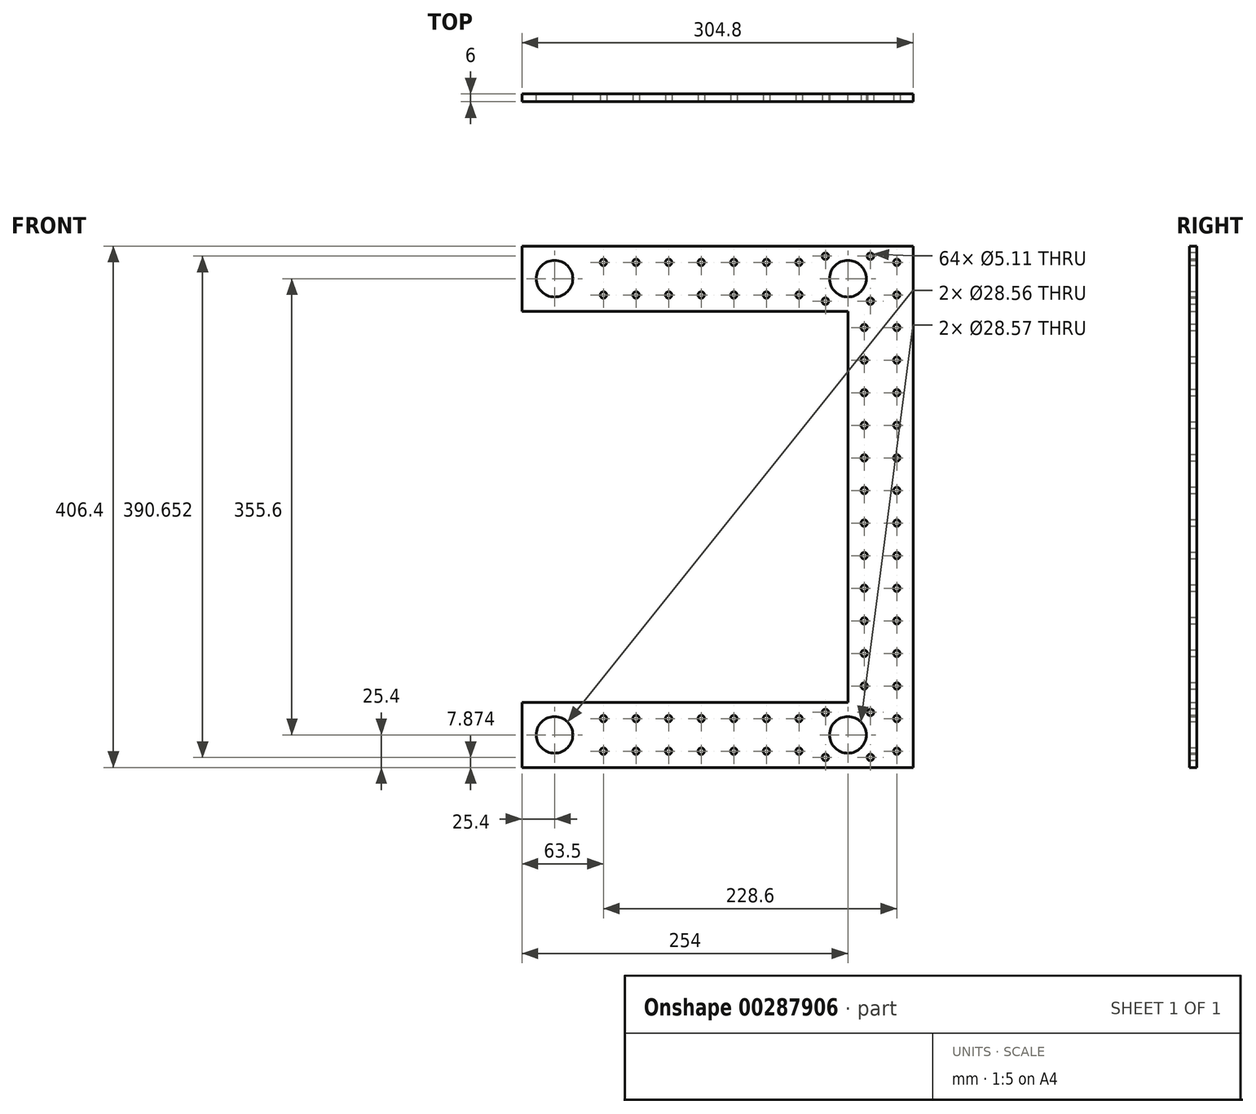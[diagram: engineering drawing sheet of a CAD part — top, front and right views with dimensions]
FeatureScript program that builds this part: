
annotation { "Feature Type Name" : "Feature", "Feature Type Description" : "" }
export const myFeature = defineFeature(function(context is Context, id is Id, definition is map)
    precondition{}
    {
        {
            var Q0;
            Q0=qCreatedBy(makeId("Front.planeOp"),FACE);
            var sketch = newSketch(context, id + "F0", { "sketchPlane" : qUnion([Q0])});
            skCircle(sketch, "E0", {"center": v(0, 0) * mm, "radius": 152.4 * mm, "construction": true});
            skLineSegment(sketch, "E1", {"start": v(0, 0) * mm, "end": v(177.8, 0) * mm, "construction": true});
            skLineSegment(sketch, "E2.bottom", {"start": v(203.2, 152.4) * mm, "end": v(152.4, 152.4) * mm, "construction": true});
            skLineSegment(sketch, "E2.top", {"start": v(203.2, -152.4) * mm, "end": v(152.4, -152.4) * mm, "construction": true});
            skLineSegment(sketch, "E2.left", {"start": v(203.2, 152.4) * mm, "end": v(203.2, -152.4) * mm});
            skLineSegment(sketch, "E2.right", {"start": v(152.4, 152.4) * mm, "end": v(152.4, -152.4) * mm});
            skPoint(sketch, "E2.middle", {"position": v(177.8, 0) * mm});
            skLineSegment(sketch, "E3", {"start": v(203.2, -152.4) * mm, "end": v(203.2, -203.2) * mm});
            skLineSegment(sketch, "E4", {"start": v(203.2, -203.2) * mm, "end": v(-101.6, -203.2) * mm});
            skLineSegment(sketch, "E5", {"start": v(-101.6, -203.2) * mm, "end": v(-101.6, -152.4) * mm});
            skLineSegment(sketch, "E6", {"start": v(-101.6, -152.4) * mm, "end": v(152.4, -152.4) * mm});
            skCircle(sketch, "E7", {"center": v(-76.2, -177.8) * mm, "radius": 14.28 * mm});
            skCircle(sketch, "E8", {"center": v(-76.2, -177.8) * mm, "radius": 38.1 * mm, "construction": true});
            skLineSegment(sketch, "E9.MirrorCS", {"start": v(-101.6, 152.4) * mm, "end": v(152.4, 152.4) * mm});
            skLineSegment(sketch, "E10.MirrorCS", {"start": v(203.2, 203.2) * mm, "end": v(-101.6, 203.2) * mm});
            skLineSegment(sketch, "E11.MirrorCS", {"start": v(203.2, 152.4) * mm, "end": v(203.2, 203.2) * mm});
            skCircle(sketch, "E12.MirrorC", {"center": v(-76.2, 177.8) * mm, "radius": 14.28 * mm});
            skCircle(sketch, "E13.MirrorC", {"center": v(-76.2, 177.8) * mm, "radius": 38.1 * mm, "construction": true});
            skLineSegment(sketch, "E14.MirrorCS", {"start": v(-101.6, 203.2) * mm, "end": v(-101.6, 152.4) * mm});
            skSolve(sketch);
        }
        {
            var Q0;
            Q0 = qSketchRegion(id + "F0", true);
            extrude(context, id + "F1", {"entities" : qUnion([Q0]), "depth" : 6 * mm});
        }
        {
            var Q0;
            Q0=makeQuery(id+"F1.opExtrude","CAP_FACE",FACE,{"disambiguationData":[OSD([sQuery(id+"F0.wireOp",EDGE,"E2.left"),sQuery(id+"F0.wireOp",EDGE,"E2.right"),sQuery(id+"F0.wireOp",EDGE,"E3"),sQuery(id+"F0.wireOp",EDGE,"E4"),sQuery(id+"F0.wireOp",EDGE,"E5"),sQuery(id+"F0.wireOp",EDGE,"E6"),sQuery(id+"F0.wireOp",EDGE,"E7"),sQuery(id+"F0.wireOp",EDGE,"E9.MirrorCS"),sQuery(id+"F0.wireOp",EDGE,"E10.MirrorCS"),sQuery(id+"F0.wireOp",EDGE,"E11.MirrorCS"),sQuery(id+"F0.wireOp",EDGE,"E12.MirrorC"),sQuery(id+"F0.wireOp",EDGE,"E14.MirrorCS")])],"isStart":false});
            var sketch = newSketch(context, id + "F2", { "sketchPlane" : qUnion([Q0])});
            skLineSegment(sketch, "E15", {"start": v(0, 0) * mm, "end": v(152.4, 0) * mm, "construction": true});
            skLineSegment(sketch, "E16", {"start": v(152.4, 152.4) * mm, "end": v(152.4, 203.2) * mm, "construction": true});
            skCircle(sketch, "E17", {"center": v(152.4, 177.8) * mm, "radius": 14.29 * mm});
            skLineSegment(sketch, "E18.bottom", {"start": v(169.93, 160.27) * mm, "end": v(134.87, 160.27) * mm, "construction": true});
            skLineSegment(sketch, "E18.top", {"start": v(169.93, 195.33) * mm, "end": v(134.87, 195.33) * mm, "construction": true});
            skLineSegment(sketch, "E18.left", {"start": v(169.93, 160.27) * mm, "end": v(169.93, 195.33) * mm, "construction": true});
            skLineSegment(sketch, "E18.right", {"start": v(134.87, 160.27) * mm, "end": v(134.87, 195.33) * mm, "construction": true});
            skCircle(sketch, "E19", {"center": v(169.93, 195.33) * mm, "radius": 2.55 * mm});
            skCircle(sketch, "E20", {"center": v(169.93, 160.27) * mm, "radius": 2.55 * mm});
            skCircle(sketch, "E21", {"center": v(134.87, 160.27) * mm, "radius": 2.55 * mm});
            skCircle(sketch, "E22", {"center": v(134.87, 195.33) * mm, "radius": 2.55 * mm});
            skCircle(sketch, "E23.MirrorC", {"center": v(134.87, -195.33) * mm, "radius": 2.55 * mm});
            skCircle(sketch, "E24.MirrorC", {"center": v(134.87, -160.27) * mm, "radius": 2.55 * mm});
            skLineSegment(sketch, "E25.MirrorCS", {"start": v(169.93, -195.33) * mm, "end": v(134.87, -195.33) * mm, "construction": true});
            skLineSegment(sketch, "E26.MirrorCS", {"start": v(169.93, -160.27) * mm, "end": v(134.87, -160.27) * mm, "construction": true});
            skCircle(sketch, "E27.MirrorC", {"center": v(169.93, -160.27) * mm, "radius": 2.55 * mm});
            skCircle(sketch, "E28.MirrorC", {"center": v(152.4, -177.8) * mm, "radius": 14.29 * mm});
            skLineSegment(sketch, "E29.MirrorCS", {"start": v(134.87, -160.27) * mm, "end": v(134.87, -195.33) * mm, "construction": true});
            skCircle(sketch, "E30.MirrorC", {"center": v(169.93, -195.33) * mm, "radius": 2.55 * mm});
            skLineSegment(sketch, "E31.MirrorCS", {"start": v(152.4, -152.4) * mm, "end": v(152.4, -203.2) * mm, "construction": true});
            skLineSegment(sketch, "E32.MirrorCS", {"start": v(169.93, -160.27) * mm, "end": v(169.93, -195.33) * mm, "construction": true});
            skSolve(sketch);
        }
        {
            var Q0;
            Q0 = qSketchRegion(id + "F2", true);
            extrude(context, id + "F3", {"entities" : qUnion([Q0]), "operationType" : NewBodyOperationType.REMOVE, "oppositeDirection" : true, "depth" : 25.4 * mm});
        }
        {
            var Q0;
            Q0=makeQuery(id+"F1.opExtrude","CAP_FACE",FACE,{"disambiguationData":[OSD([sQuery(id+"F0.wireOp",EDGE,"E2.left"),sQuery(id+"F0.wireOp",EDGE,"E2.right"),sQuery(id+"F0.wireOp",EDGE,"E3"),sQuery(id+"F0.wireOp",EDGE,"E4"),sQuery(id+"F0.wireOp",EDGE,"E5"),sQuery(id+"F0.wireOp",EDGE,"E6"),sQuery(id+"F0.wireOp",EDGE,"E7"),sQuery(id+"F0.wireOp",EDGE,"E9.MirrorCS"),sQuery(id+"F0.wireOp",EDGE,"E10.MirrorCS"),sQuery(id+"F0.wireOp",EDGE,"E11.MirrorCS"),sQuery(id+"F0.wireOp",EDGE,"E12.MirrorC"),sQuery(id+"F0.wireOp",EDGE,"E14.MirrorCS")])],"isStart":false});
            var sketch = newSketch(context, id + "F4", { "sketchPlane" : qUnion([Q0])});
            skCircle(sketch, "E33", {"center": v(-88.9, 190.5) * mm, "radius": 2.55 * mm, "construction": true});
            skCircle(sketch, "E34.0.1.0", {"center": v(-88.9, 165.1) * mm, "radius": 2.55 * mm, "construction": true});
            skCircle(sketch, "E34.1.0.0", {"center": v(-63.5, 190.5) * mm, "radius": 2.55 * mm, "construction": true});
            skCircle(sketch, "E34.1.1.0", {"center": v(-63.5, 165.1) * mm, "radius": 2.55 * mm, "construction": true});
            skCircle(sketch, "E34.2.0.0", {"center": v(-38.1, 190.5) * mm, "radius": 2.55 * mm});
            skCircle(sketch, "E34.2.1.0", {"center": v(-38.1, 165.1) * mm, "radius": 2.55 * mm});
            skCircle(sketch, "E34.3.0.0", {"center": v(-12.7, 190.5) * mm, "radius": 2.55 * mm});
            skCircle(sketch, "E34.3.1.0", {"center": v(-12.7, 165.1) * mm, "radius": 2.55 * mm});
            skCircle(sketch, "E34.4.0.0", {"center": v(12.7, 190.5) * mm, "radius": 2.55 * mm});
            skCircle(sketch, "E34.4.1.0", {"center": v(12.7, 165.1) * mm, "radius": 2.55 * mm});
            skCircle(sketch, "E34.5.0.0", {"center": v(38.1, 190.5) * mm, "radius": 2.55 * mm});
            skCircle(sketch, "E34.5.1.0", {"center": v(38.1, 165.1) * mm, "radius": 2.55 * mm});
            skCircle(sketch, "E34.6.0.0", {"center": v(63.5, 190.5) * mm, "radius": 2.55 * mm});
            skCircle(sketch, "E34.6.1.0", {"center": v(63.5, 165.1) * mm, "radius": 2.55 * mm});
            skCircle(sketch, "E34.7.0.0", {"center": v(88.9, 190.5) * mm, "radius": 2.55 * mm});
            skCircle(sketch, "E34.7.1.0", {"center": v(88.9, 165.1) * mm, "radius": 2.55 * mm});
            skCircle(sketch, "E34.8.0.0", {"center": v(114.3, 190.5) * mm, "radius": 2.55 * mm});
            skCircle(sketch, "E34.8.1.0", {"center": v(114.3, 165.1) * mm, "radius": 2.55 * mm});
            skCircle(sketch, "E34.9.0.0", {"center": v(139.7, 190.5) * mm, "radius": 2.55 * mm, "construction": true});
            skCircle(sketch, "E34.9.1.0", {"center": v(139.7, 165.1) * mm, "radius": 2.55 * mm, "construction": true});
            skCircle(sketch, "E34.10.0.0", {"center": v(165.1, 190.5) * mm, "radius": 2.55 * mm, "construction": true});
            skCircle(sketch, "E34.10.1.0", {"center": v(165.1, 165.1) * mm, "radius": 2.55 * mm, "construction": true});
            skCircle(sketch, "E34.11.0.0", {"center": v(190.5, 190.5) * mm, "radius": 2.55 * mm});
            skCircle(sketch, "E34.11.1.0", {"center": v(190.5, 165.1) * mm, "radius": 2.55 * mm});
            skLineSegment(sketch, "E34.direction1", {"start": v(-88.9, 190.5) * mm, "end": v(-63.5, 190.5) * mm, "construction": true});
            skLineSegment(sketch, "E34.direction2", {"start": v(-88.9, 190.5) * mm, "end": v(-88.9, 165.1) * mm, "construction": true});
            skLineSegment(sketch, "E35", {"start": v(0, 0) * mm, "end": v(152.4, 0) * mm, "construction": true});
            skCircle(sketch, "E36.MirrorC", {"center": v(165.1, -165.1) * mm, "radius": 2.55 * mm, "construction": true});
            skCircle(sketch, "E37.MirrorC", {"center": v(-88.9, -190.5) * mm, "radius": 2.55 * mm, "construction": true});
            skCircle(sketch, "E38.MirrorC", {"center": v(88.9, -190.5) * mm, "radius": 2.55 * mm});
            skCircle(sketch, "E39.MirrorC", {"center": v(-38.1, -190.5) * mm, "radius": 2.55 * mm});
            skCircle(sketch, "E40.MirrorC", {"center": v(139.7, -190.5) * mm, "radius": 2.55 * mm, "construction": true});
            skLineSegment(sketch, "E41.MirrorCS", {"start": v(-88.9, -190.5) * mm, "end": v(-63.5, -190.5) * mm, "construction": true});
            skCircle(sketch, "E42.MirrorC", {"center": v(38.1, -190.5) * mm, "radius": 2.55 * mm});
            skCircle(sketch, "E43.MirrorC", {"center": v(-88.9, -165.1) * mm, "radius": 2.55 * mm, "construction": true});
            skCircle(sketch, "E44.MirrorC", {"center": v(88.9, -165.1) * mm, "radius": 2.55 * mm});
            skCircle(sketch, "E45.MirrorC", {"center": v(-12.7, -165.1) * mm, "radius": 2.55 * mm});
            skCircle(sketch, "E46.MirrorC", {"center": v(-38.1, -165.1) * mm, "radius": 2.55 * mm});
            skCircle(sketch, "E47.MirrorC", {"center": v(165.1, -190.5) * mm, "radius": 2.55 * mm, "construction": true});
            skCircle(sketch, "E48.MirrorC", {"center": v(38.1, -165.1) * mm, "radius": 2.55 * mm});
            skCircle(sketch, "E49.MirrorC", {"center": v(-63.5, -190.5) * mm, "radius": 2.55 * mm, "construction": true});
            skCircle(sketch, "E50.MirrorC", {"center": v(114.3, -165.1) * mm, "radius": 2.55 * mm});
            skCircle(sketch, "E51.MirrorC", {"center": v(190.5, -190.5) * mm, "radius": 2.55 * mm});
            skCircle(sketch, "E52.MirrorC", {"center": v(190.5, -165.1) * mm, "radius": 2.55 * mm});
            skCircle(sketch, "E53.MirrorC", {"center": v(12.7, -190.5) * mm, "radius": 2.55 * mm});
            skCircle(sketch, "E54.MirrorC", {"center": v(-12.7, -190.5) * mm, "radius": 2.55 * mm});
            skCircle(sketch, "E55.MirrorC", {"center": v(63.5, -165.1) * mm, "radius": 2.55 * mm});
            skCircle(sketch, "E56.MirrorC", {"center": v(139.7, -165.1) * mm, "radius": 2.55 * mm, "construction": true});
            skCircle(sketch, "E57.MirrorC", {"center": v(63.5, -190.5) * mm, "radius": 2.55 * mm});
            skLineSegment(sketch, "E58.MirrorCS", {"start": v(-88.9, -190.5) * mm, "end": v(-88.9, -165.1) * mm, "construction": true});
            skCircle(sketch, "E59.MirrorC", {"center": v(-63.5, -165.1) * mm, "radius": 2.55 * mm, "construction": true});
            skCircle(sketch, "E60.MirrorC", {"center": v(12.7, -165.1) * mm, "radius": 2.55 * mm});
            skCircle(sketch, "E61.MirrorC", {"center": v(114.3, -190.5) * mm, "radius": 2.55 * mm});
            skCircle(sketch, "E62.0.1.0", {"center": v(190.5, 139.7) * mm, "radius": 2.55 * mm});
            skCircle(sketch, "E62.0.2.0", {"center": v(190.5, 114.3) * mm, "radius": 2.55 * mm});
            skCircle(sketch, "E62.0.3.0", {"center": v(190.5, 88.9) * mm, "radius": 2.55 * mm});
            skCircle(sketch, "E62.0.4.0", {"center": v(190.5, 63.5) * mm, "radius": 2.55 * mm});
            skCircle(sketch, "E62.0.5.0", {"center": v(190.5, 38.1) * mm, "radius": 2.55 * mm});
            skCircle(sketch, "E62.0.6.0", {"center": v(190.5, 12.7) * mm, "radius": 2.55 * mm});
            skCircle(sketch, "E62.0.7.0", {"center": v(190.5, -12.7) * mm, "radius": 2.55 * mm});
            skCircle(sketch, "E62.0.8.0", {"center": v(190.5, -38.1) * mm, "radius": 2.55 * mm});
            skCircle(sketch, "E62.0.9.0", {"center": v(190.5, -63.5) * mm, "radius": 2.55 * mm});
            skCircle(sketch, "E62.0.10.0", {"center": v(190.5, -88.9) * mm, "radius": 2.55 * mm});
            skCircle(sketch, "E62.0.11.0", {"center": v(190.5, -114.3) * mm, "radius": 2.55 * mm});
            skCircle(sketch, "E62.0.12.0", {"center": v(190.5, -139.7) * mm, "radius": 2.55 * mm});
            skCircle(sketch, "E62.1.0.0", {"center": v(165.1, 165.1) * mm, "radius": 2.55 * mm});
            skCircle(sketch, "E62.1.1.0", {"center": v(165.1, 139.7) * mm, "radius": 2.55 * mm});
            skCircle(sketch, "E62.1.2.0", {"center": v(165.1, 114.3) * mm, "radius": 2.55 * mm});
            skCircle(sketch, "E62.1.3.0", {"center": v(165.1, 88.9) * mm, "radius": 2.55 * mm});
            skCircle(sketch, "E62.1.4.0", {"center": v(165.1, 63.5) * mm, "radius": 2.55 * mm});
            skCircle(sketch, "E62.1.5.0", {"center": v(165.1, 38.1) * mm, "radius": 2.55 * mm});
            skCircle(sketch, "E62.1.6.0", {"center": v(165.1, 12.7) * mm, "radius": 2.55 * mm});
            skCircle(sketch, "E62.1.7.0", {"center": v(165.1, -12.7) * mm, "radius": 2.55 * mm});
            skCircle(sketch, "E62.1.8.0", {"center": v(165.1, -38.1) * mm, "radius": 2.55 * mm});
            skCircle(sketch, "E62.1.9.0", {"center": v(165.1, -63.5) * mm, "radius": 2.55 * mm});
            skCircle(sketch, "E62.1.10.0", {"center": v(165.1, -88.9) * mm, "radius": 2.55 * mm});
            skCircle(sketch, "E62.1.11.0", {"center": v(165.1, -114.3) * mm, "radius": 2.55 * mm});
            skCircle(sketch, "E62.1.12.0", {"center": v(165.1, -139.7) * mm, "radius": 2.55 * mm});
            skLineSegment(sketch, "E62.direction1", {"start": v(190.5, 165.1) * mm, "end": v(165.1, 165.1) * mm, "construction": true});
            skLineSegment(sketch, "E62.direction2", {"start": v(190.5, 165.1) * mm, "end": v(190.5, 139.7) * mm, "construction": true});
            skSolve(sketch);
        }
        {
            var Q0;
            Q0=sQuery(id+"F4.wireOp",VERTEX,"E34.8.0.0.center");
            var Q1;
            Q1=sQuery(id+"F4.wireOp",VERTEX,"E34.8.1.0.center");
            var Q2;
            Q2=sQuery(id+"F4.wireOp",VERTEX,"E34.7.1.0.center");
            var Q3;
            Q3=sQuery(id+"F4.wireOp",VERTEX,"E34.2.0.0.center");
            var Q4;
            Q4=sQuery(id+"F4.wireOp",VERTEX,"E34.4.0.0.center");
            var Q5;
            Q5=sQuery(id+"F4.wireOp",VERTEX,"E34.6.1.0.center");
            var Q6;
            Q6=sQuery(id+"F4.wireOp",VERTEX,"E34.7.0.0.center");
            var Q7;
            Q7=sQuery(id+"F4.wireOp",VERTEX,"E34.6.0.0.center");
            var Q8;
            Q8=sQuery(id+"F4.wireOp",VERTEX,"E34.2.1.0.center");
            var Q9;
            Q9=sQuery(id+"F4.wireOp",VERTEX,"E34.5.1.0.center");
            var Q10;
            Q10=sQuery(id+"F4.wireOp",VERTEX,"E34.5.0.0.center");
            var Q11;
            Q11=sQuery(id+"F4.wireOp",VERTEX,"E34.3.0.0.center");
            var Q12;
            Q12=sQuery(id+"F4.wireOp",VERTEX,"E34.4.1.0.center");
            var Q13;
            Q13=sQuery(id+"F4.wireOp",VERTEX,"E34.3.1.0.center");
            var Q14;
            Q14=sQuery(id+"F4.wireOp",VERTEX,"E34.11.1.0.center");
            var Q15;
            Q15=sQuery(id+"F4.wireOp",VERTEX,"E34.11.0.0.center");
            var Q16;
            Q16=sQuery(id+"F4.wireOp",VERTEX,"E50.MirrorC.center");
            var Q17;
            Q17=sQuery(id+"F4.wireOp",VERTEX,"E39.MirrorC.center");
            var Q18;
            Q18=sQuery(id+"F4.wireOp",VERTEX,"E45.MirrorC.center");
            var Q19;
            Q19=sQuery(id+"F4.wireOp",VERTEX,"E48.MirrorC.center");
            var Q20;
            Q20=sQuery(id+"F4.wireOp",VERTEX,"E46.MirrorC.center");
            var Q21;
            Q21=sQuery(id+"F4.wireOp",VERTEX,"E54.MirrorC.center");
            var Q22;
            Q22=sQuery(id+"F4.wireOp",VERTEX,"E38.MirrorC.center");
            var Q23;
            Q23=sQuery(id+"F4.wireOp",VERTEX,"E53.MirrorC.center");
            var Q24;
            Q24=sQuery(id+"F4.wireOp",VERTEX,"E55.MirrorC.center");
            var Q25;
            Q25=sQuery(id+"F4.wireOp",VERTEX,"E60.MirrorC.center");
            var Q26;
            Q26=sQuery(id+"F4.wireOp",VERTEX,"E61.MirrorC.center");
            var Q27;
            Q27=sQuery(id+"F4.wireOp",VERTEX,"E44.MirrorC.center");
            var Q28;
            Q28=sQuery(id+"F4.wireOp",VERTEX,"E42.MirrorC.center");
            var Q29;
            Q29=sQuery(id+"F4.wireOp",VERTEX,"E57.MirrorC.center");
            var Q30;
            Q30=sQuery(id+"F4.wireOp",VERTEX,"E52.MirrorC.center");
            var Q31;
            Q31=sQuery(id+"F4.wireOp",VERTEX,"E51.MirrorC.center");
            var Q32;
            Q32=sQuery(id+"F4.wireOp",VERTEX,"E62.0.1.0.center");
            var Q33;
            Q33=sQuery(id+"F4.wireOp",VERTEX,"E62.1.1.0.center");
            var Q34;
            Q34=sQuery(id+"F4.wireOp",VERTEX,"E62.0.2.0.center");
            var Q35;
            Q35=sQuery(id+"F4.wireOp",VERTEX,"E62.1.2.0.center");
            var Q36;
            Q36=sQuery(id+"F4.wireOp",VERTEX,"E62.0.3.0.center");
            var Q37;
            Q37=sQuery(id+"F4.wireOp",VERTEX,"E62.1.3.0.center");
            var Q38;
            Q38=sQuery(id+"F4.wireOp",VERTEX,"E62.0.4.0.center");
            var Q39;
            Q39=sQuery(id+"F4.wireOp",VERTEX,"E62.1.4.0.center");
            var Q40;
            Q40=sQuery(id+"F4.wireOp",VERTEX,"E62.0.5.0.center");
            var Q41;
            Q41=sQuery(id+"F4.wireOp",VERTEX,"E62.1.5.0.center");
            var Q42;
            Q42=sQuery(id+"F4.wireOp",VERTEX,"E62.0.6.0.center");
            var Q43;
            Q43=sQuery(id+"F4.wireOp",VERTEX,"E62.1.6.0.center");
            var Q44;
            Q44=sQuery(id+"F4.wireOp",VERTEX,"E62.0.7.0.center");
            var Q45;
            Q45=sQuery(id+"F4.wireOp",VERTEX,"E62.1.7.0.center");
            var Q46;
            Q46=sQuery(id+"F4.wireOp",VERTEX,"E62.0.8.0.center");
            var Q47;
            Q47=sQuery(id+"F4.wireOp",VERTEX,"E62.1.8.0.center");
            var Q48;
            Q48=sQuery(id+"F4.wireOp",VERTEX,"E62.0.9.0.center");
            var Q49;
            Q49=sQuery(id+"F4.wireOp",VERTEX,"E62.1.9.0.center");
            var Q50;
            Q50=sQuery(id+"F4.wireOp",VERTEX,"E62.0.10.0.center");
            var Q51;
            Q51=sQuery(id+"F4.wireOp",VERTEX,"E62.1.10.0.center");
            var Q52;
            Q52=sQuery(id+"F4.wireOp",VERTEX,"E62.0.11.0.center");
            var Q53;
            Q53=sQuery(id+"F4.wireOp",VERTEX,"E62.1.11.0.center");
            var Q54;
            Q54=sQuery(id+"F4.wireOp",VERTEX,"E62.0.12.0.center");
            var Q55;
            Q55=sQuery(id+"F4.wireOp",VERTEX,"E62.1.12.0.center");
            var Q56;
            Q56=makeQuery(id+"F1.opExtrude","SWEPT_BODY",BODY,{"disambiguationData":[OSD([sQuery(id+"F0.wireOp",EDGE,"E2.left"),sQuery(id+"F0.wireOp",EDGE,"E2.right"),sQuery(id+"F0.wireOp",EDGE,"E3"),sQuery(id+"F0.wireOp",EDGE,"E4"),sQuery(id+"F0.wireOp",EDGE,"E5"),sQuery(id+"F0.wireOp",EDGE,"E6"),sQuery(id+"F0.wireOp",EDGE,"E7"),sQuery(id+"F0.wireOp",EDGE,"E9.MirrorCS"),sQuery(id+"F0.wireOp",EDGE,"E10.MirrorCS"),sQuery(id+"F0.wireOp",EDGE,"E11.MirrorCS"),sQuery(id+"F0.wireOp",EDGE,"E12.MirrorC"),sQuery(id+"F0.wireOp",EDGE,"E14.MirrorCS")])]});
            hole(context, id + "F5", {"style" : HoleStyle.SIMPLE, "endStyle" : HoleEndStyle.THROUGH, "holeDiameter" : 5.1 * mm, "tappedDepth" : 12.7 * mm, "tapClearance" : 3, "locations" : qUnion([Q0, Q1, Q2, Q3, Q4, Q5, Q6, Q7, Q8, Q9, Q10, Q11, Q12, Q13, Q14, Q15, Q16, Q17, Q18, Q19, Q20, Q21, Q22, Q23, Q24, Q25, Q26, Q27, Q28, Q29, Q30, Q31, Q32, Q33, Q34, Q35, Q36, Q37, Q38, Q39, Q40, Q41, Q42, Q43, Q44, Q45, Q46, Q47, Q48, Q49, Q50, Q51, Q52, Q53, Q54, Q55]), "scope" : qUnion([Q56])});
        }
    });
